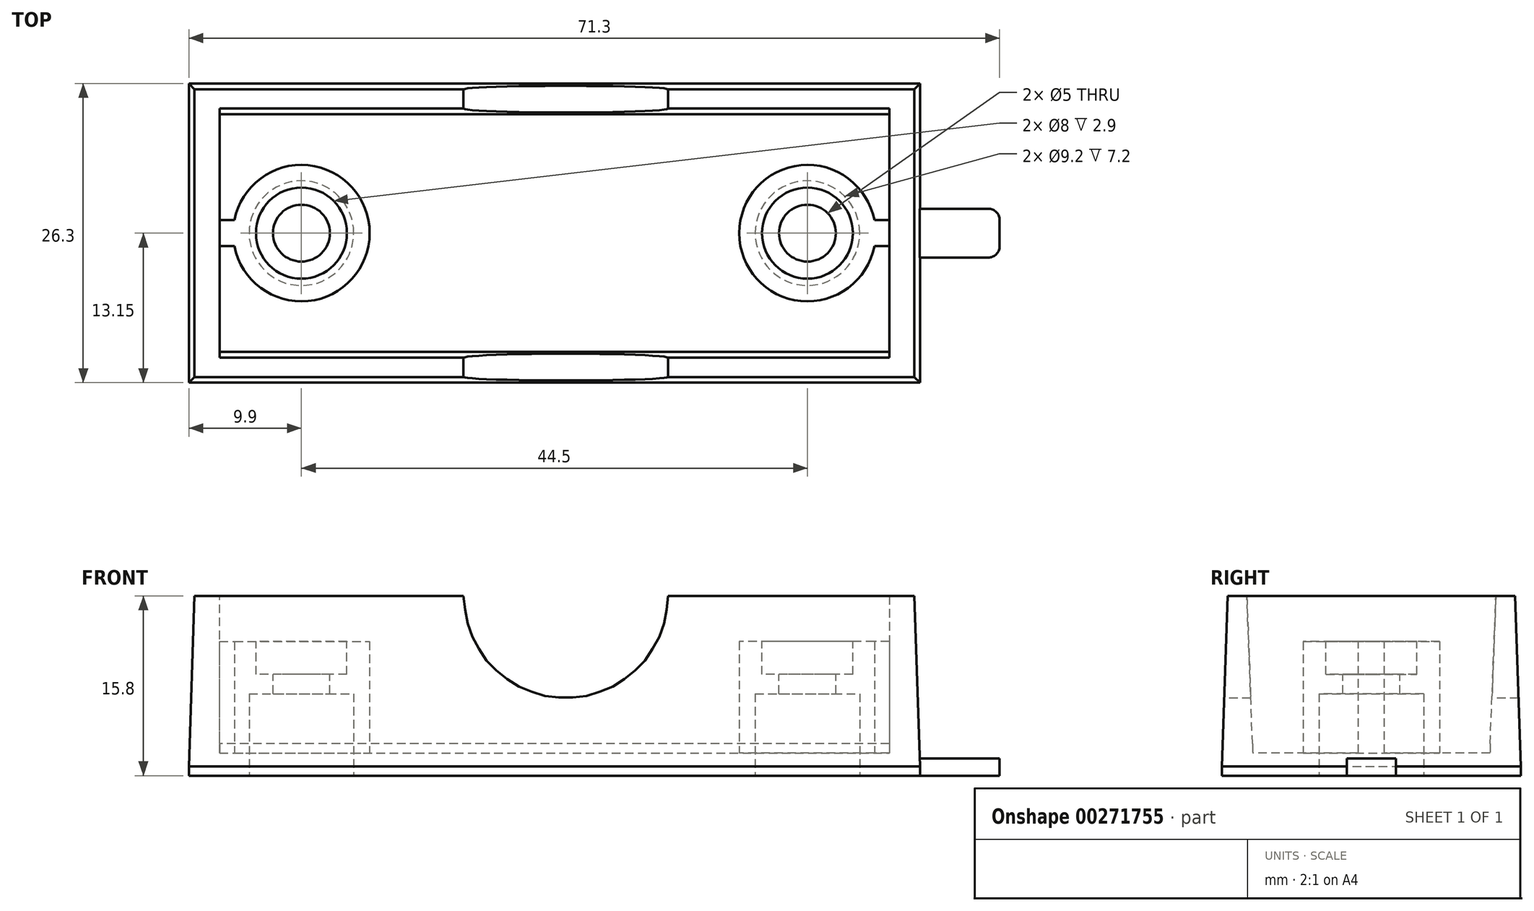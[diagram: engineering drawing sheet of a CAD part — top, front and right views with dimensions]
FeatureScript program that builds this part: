
annotation { "Feature Type Name" : "Feature", "Feature Type Description" : "" }
export const myFeature = defineFeature(function(context is Context, id is Id, definition is map)
    precondition{}
    {
        {
            var Q0;
            Q0=qCreatedBy(makeId("Top.planeOp"),FACE);
            var sketch = newSketch(context, id + "F0", { "sketchPlane" : qUnion([Q0])});
            skLineSegment(sketch, "E0.bottom", {"start": v(-32.15, 13.15) * mm, "end": v(32.15, 13.15) * mm});
            skLineSegment(sketch, "E0.top", {"start": v(-32.15, -13.15) * mm, "end": v(32.15, -13.15) * mm});
            skLineSegment(sketch, "E0.left", {"start": v(-32.15, 13.15) * mm, "end": v(-32.15, -13.15) * mm});
            skLineSegment(sketch, "E0.right", {"start": v(32.15, 13.15) * mm, "end": v(32.15, -13.15) * mm});
            skSolve(sketch);
        }
        {
            var Q0;
            Q0 = qSketchRegion(id + "F0", true);
            extrude(context, id + "F1", {"entities" : qUnion([Q0]), "depth" : 2 * mm});
        }
        {
            var Q0;
            Q0=makeQuery(id+"F1.opExtrude","CAP_FACE",FACE,{"disambiguationData":[OSD([sQuery(id+"F0.wireOp",EDGE,"E0.bottom"),sQuery(id+"F0.wireOp",EDGE,"E0.top"),sQuery(id+"F0.wireOp",EDGE,"E0.left"),sQuery(id+"F0.wireOp",EDGE,"E0.right")])],"isStart":false});
            var sketch = newSketch(context, id + "F2", { "sketchPlane" : qUnion([Q0])});
            skLineSegment(sketch, "E1.bottom", {"start": v(-32.15, 13.15) * mm, "end": v(32.15, 13.15) * mm});
            skLineSegment(sketch, "E1.top", {"start": v(-32.15, -13.15) * mm, "end": v(32.15, -13.15) * mm});
            skLineSegment(sketch, "E1.left", {"start": v(-32.15, 13.15) * mm, "end": v(-32.15, -13.15) * mm});
            skLineSegment(sketch, "E1.right", {"start": v(32.15, 13.15) * mm, "end": v(32.15, -13.15) * mm});
            skLineSegment(sketch, "E2.bottom", {"start": v(-29.45, 10.45) * mm, "end": v(29.45, 10.45) * mm});
            skLineSegment(sketch, "E2.top", {"start": v(-29.45, -10.45) * mm, "end": v(29.45, -10.45) * mm});
            skLineSegment(sketch, "E2.left", {"start": v(-29.45, 10.45) * mm, "end": v(-29.45, -10.45) * mm});
            skLineSegment(sketch, "E2.right", {"start": v(29.45, 10.45) * mm, "end": v(29.45, -10.45) * mm});
            skSolve(sketch);
        }
        {
            var Q0;
            Q0 = qSketchRegion(id + "F2", true);
            extrude(context, id + "F3", {"entities" : qUnion([Q0]), "operationType" : NewBodyOperationType.ADD, "depth" : 13.8 * mm});
        }
        {
            var Q0;
            Q0=makeQuery(id+"F3.boolean.opBoolean","MERGE",FACE,{"derivedFrom":[makeQuery(id+"F1.opExtrude","SWEPT_FACE",FACE,{"disambiguationData":[OSD([sQuery(id+"F0.wireOp",EDGE,"E0.top")])]}),makeQuery(id+"F3.opExtrude","SWEPT_FACE",FACE,{"disambiguationData":[OSD([sQuery(id+"F2.wireOp",EDGE,"E1.top")])]})]});
            var sketch = newSketch(context, id + "F4", { "sketchPlane" : qUnion([Q0])});
            skArc(sketch, "E3", {"start": v(10, 15.8) * mm, "mid": v(1, 6.8) * mm, "end": v(-8, 15.8) * mm});
            skLineSegment(sketch, "E4", {"start": v(-8, 15.8) * mm, "end": v(10, 15.8) * mm});
            skSolve(sketch);
        }
        {
            var Q0;
            Q0 = qSketchRegion(id + "F4", true);
            extrude(context, id + "F5", {"entities" : qUnion([Q0]), "operationType" : NewBodyOperationType.REMOVE, "oppositeDirection" : true, "depth" : 26.5 * mm});
        }
        {
            var Q0;
            Q0=makeQuery(id+"F1.opExtrude","CAP_FACE",FACE,{"disambiguationData":[OSD([sQuery(id+"F0.wireOp",EDGE,"E0.bottom"),sQuery(id+"F0.wireOp",EDGE,"E0.top"),sQuery(id+"F0.wireOp",EDGE,"E0.left"),sQuery(id+"F0.wireOp",EDGE,"E0.right")])],"isStart":false});
            var sketch = newSketch(context, id + "F6", { "sketchPlane" : qUnion([Q0])});
            skCircle(sketch, "E5", {"center": v(-22.25, 0) * mm, "radius": 6 * mm});
            skCircle(sketch, "E6", {"center": v(22.25, 0) * mm, "radius": 6 * mm});
            skLineSegment(sketch, "E7.top", {"start": v(-28.14, -1.15) * mm, "end": v(-29.45, -1.15) * mm});
            skLineSegment(sketch, "E7.left", {"start": v(-28.14, 1.15) * mm, "end": v(-28.14, -1.15) * mm});
            skLineSegment(sketch, "E8.bottom", {"start": v(-30.88, 1.15) * mm, "end": v(-28.14, 1.15) * mm});
            skLineSegment(sketch, "E8.top", {"start": v(-30.88, -1.15) * mm, "end": v(-28.14, -1.15) * mm});
            skLineSegment(sketch, "E8.left", {"start": v(-30.88, 1.15) * mm, "end": v(-30.88, -1.15) * mm});
            skLineSegment(sketch, "E9.bottom", {"start": v(29.95, 1.15) * mm, "end": v(28.14, 1.15) * mm});
            skLineSegment(sketch, "E9.top", {"start": v(29.95, -1.15) * mm, "end": v(28.14, -1.15) * mm});
            skLineSegment(sketch, "E9.left", {"start": v(29.95, 1.15) * mm, "end": v(29.95, -1.15) * mm});
            skLineSegment(sketch, "E9.right", {"start": v(28.14, 1.15) * mm, "end": v(28.14, -1.15) * mm});
            skSolve(sketch);
        }
        {
            var Q0;
            Q0 = qSketchRegion(id + "F6", true);
            extrude(context, id + "F7", {"entities" : qUnion([Q0]), "operationType" : NewBodyOperationType.ADD, "depth" : 9.8 * mm});
        }
        {
            var Q0;
            Q0=makeQuery(id+"F7.opExtrude","CAP_FACE",FACE,{"disambiguationData":[OSD([sQuery(id+"F6.wireOp",EDGE,"E5"),sQuery(id+"F6.wireOp",EDGE,"E8.bottom"),sQuery(id+"F6.wireOp",EDGE,"E8.top"),sQuery(id+"F6.wireOp",EDGE,"E8.left")])],"isStart":false});
            var sketch = newSketch(context, id + "F8", { "sketchPlane" : qUnion([Q0])});
            skCircle(sketch, "E10", {"center": v(-22.25, 0) * mm, "radius": 4 * mm});
            skSolve(sketch);
        }
        {
            var Q0;
            Q0 = qSketchRegion(id + "F8", true);
            extrude(context, id + "F9", {"entities" : qUnion([Q0]), "operationType" : NewBodyOperationType.REMOVE, "oppositeDirection" : true, "depth" : 2.9 * mm});
        }
        {
            var Q0;
            Q0=makeQuery(id+"F7.opExtrude","CAP_FACE",FACE,{"disambiguationData":[OSD([sQuery(id+"F6.wireOp",EDGE,"E6"),sQuery(id+"F6.wireOp",EDGE,"E9.bottom"),sQuery(id+"F6.wireOp",EDGE,"E9.top"),sQuery(id+"F6.wireOp",EDGE,"E9.left")])],"isStart":false});
            var sketch = newSketch(context, id + "F10", { "sketchPlane" : qUnion([Q0])});
            skCircle(sketch, "E11", {"center": v(22.25, 0) * mm, "radius": 4 * mm});
            skSolve(sketch);
        }
        {
            var Q0;
            Q0 = qSketchRegion(id + "F10", true);
            extrude(context, id + "F11", {"entities" : qUnion([Q0]), "operationType" : NewBodyOperationType.REMOVE, "oppositeDirection" : true, "depth" : 2.9 * mm});
        }
        {
            var Q0;
            Q0=makeQuery(id+"F9.boolean.opBoolean","COPY",FACE,{"derivedFrom":makeQuery(id+"F9.opExtrude","CAP_FACE",FACE,{"disambiguationData":[OSD([sQuery(id+"F8.wireOp",EDGE,"E10")])],"isStart":false})});
            var sketch = newSketch(context, id + "F12", { "sketchPlane" : qUnion([Q0])});
            skCircle(sketch, "E12", {"center": v(-22.25, 0) * mm, "radius": 2.5 * mm});
            skSolve(sketch);
        }
        {
            var Q0;
            Q0 = qSketchRegion(id + "F12", true);
            extrude(context, id + "F13", {"entities" : qUnion([Q0]), "operationType" : NewBodyOperationType.REMOVE, "oppositeDirection" : true, "depth" : 9 * mm});
        }
        {
            var Q0;
            Q0=makeQuery(id+"F11.boolean.opBoolean","COPY",FACE,{"derivedFrom":makeQuery(id+"F11.opExtrude","CAP_FACE",FACE,{"disambiguationData":[OSD([sQuery(id+"F10.wireOp",EDGE,"E11")])],"isStart":false})});
            var sketch = newSketch(context, id + "F14", { "sketchPlane" : qUnion([Q0])});
            skCircle(sketch, "E13", {"center": v(22.25, 0) * mm, "radius": 2.5 * mm});
            skSolve(sketch);
        }
        {
            var Q0;
            Q0 = qSketchRegion(id + "F14", true);
            extrude(context, id + "F15", {"entities" : qUnion([Q0]), "operationType" : NewBodyOperationType.REMOVE, "oppositeDirection" : true, "depth" : 9 * mm});
        }
        {
            var Q0;
            Q0=makeQuery(id+"F1.opExtrude","CAP_FACE",FACE,{"disambiguationData":[OSD([sQuery(id+"F0.wireOp",EDGE,"E0.bottom"),sQuery(id+"F0.wireOp",EDGE,"E0.top"),sQuery(id+"F0.wireOp",EDGE,"E0.left"),sQuery(id+"F0.wireOp",EDGE,"E0.right")])],"isStart":true});
            var sketch = newSketch(context, id + "F16", { "sketchPlane" : qUnion([Q0])});
            skCircle(sketch, "E14", {"center": v(-22.25, 0) * mm, "radius": 4.6 * mm});
            skCircle(sketch, "E15", {"center": v(22.25, 0) * mm, "radius": 4.6 * mm});
            skSolve(sketch);
        }
        {
            var Q0;
            Q0 = qSketchRegion(id + "F16", true);
            extrude(context, id + "F17", {"entities" : qUnion([Q0]), "operationType" : NewBodyOperationType.REMOVE, "oppositeDirection" : true, "depth" : 7.2 * mm});
        }
        {
            var Q0;
            {var subQ0=sQuery(id+"F2.wireOp",EDGE,"E1.bottom");Q0=makeQuery(id+"F5.boolean.opBoolean","SPLIT",EDGE,{"disambiguationData":[TD([makeQuery(id+"F1.opExtrude","SWEPT_FACE",FACE,{"disambiguationData":[OSD([sQuery(id+"F0.wireOp",EDGE,"E0.left")])]})])],"derivedFrom":makeQuery(id+"F3.opExtrude","CAP_EDGE",EDGE,{"disambiguationData":[OSD([subQ0])],"isStart":false})});}
            var Q1;
            {var subQ0=sQuery(id+"F2.wireOp",EDGE,"E1.top");Q1=makeQuery(id+"F5.boolean.opBoolean","SPLIT",EDGE,{"disambiguationData":[TD([makeQuery(id+"F1.opExtrude","SWEPT_FACE",FACE,{"disambiguationData":[OSD([sQuery(id+"F0.wireOp",EDGE,"E0.left")])]})])],"derivedFrom":makeQuery(id+"F3.opExtrude","CAP_EDGE",EDGE,{"disambiguationData":[OSD([subQ0])],"isStart":false})});}
            var Q2;
            Q2=makeQuery(id+"F3.opExtrude","CAP_EDGE",EDGE,{"disambiguationData":[OSD([sQuery(id+"F2.wireOp",EDGE,"E1.right")])],"isStart":false});
            var Q3;
            Q3=makeQuery(id+"F3.opExtrude","CAP_EDGE",EDGE,{"disambiguationData":[OSD([sQuery(id+"F2.wireOp",EDGE,"E1.left")])],"isStart":false});
            chamfer(context, id + "F18", {"entities" : qUnion([Q0, Q1, Q2, Q3]), "chamferType" : ChamferType.TWO_OFFSETS, "width1" : 15 * mm, "oppositeDirection" : false, "width2" : .5 * mm, "tangentPropagation" : true});
        }
        {
            var Q0;
            {var subQ0=sQuery(id+"F2.wireOp",EDGE,"E2.right");var subQ1=sQuery(id+"F2.wireOp",EDGE,"E2.top");Q0=makeQuery(id+"F5.boolean.opBoolean","SPLIT",EDGE,{"disambiguationData":[TD([makeQuery(id+"F3.opExtrude","SWEPT_FACE",FACE,{"disambiguationData":[OSD([subQ0])]})])],"derivedFrom":makeQuery(id+"F3.opExtrude","CAP_EDGE",EDGE,{"disambiguationData":[OSD([subQ1])],"isStart":false})});}
            var Q1;
            {var subQ0=sQuery(id+"F2.wireOp",EDGE,"E2.right");var subQ1=sQuery(id+"F2.wireOp",EDGE,"E2.bottom");Q1=makeQuery(id+"F5.boolean.opBoolean","SPLIT",EDGE,{"disambiguationData":[TD([makeQuery(id+"F3.opExtrude","SWEPT_FACE",FACE,{"disambiguationData":[OSD([subQ0])]})])],"derivedFrom":makeQuery(id+"F3.opExtrude","CAP_EDGE",EDGE,{"disambiguationData":[OSD([subQ1])],"isStart":false})});}
            chamfer(context, id + "F19", {"entities" : qUnion([Q0, Q1]), "chamferType" : ChamferType.TWO_OFFSETS, "width1" : 13 * mm, "oppositeDirection" : false, "width2" : .5 * mm, "tangentPropagation" : true});
        }
        {
            var Q0;
            Q0=qCreatedBy(makeId("Top.planeOp"),FACE);
            var sketch = newSketch(context, id + "F20", { "sketchPlane" : qUnion([Q0])});
            skLineSegment(sketch, "E16.bottom", {"start": v(39.15, 2.15) * mm, "end": v(31, 2.15) * mm});
            skLineSegment(sketch, "E16.top", {"start": v(39.15, -2.15) * mm, "end": v(31, -2.15) * mm});
            skLineSegment(sketch, "E16.left", {"start": v(39.15, 2.15) * mm, "end": v(39.15, -2.15) * mm});
            skLineSegment(sketch, "E16.right", {"start": v(31, 2.15) * mm, "end": v(31, -2.15) * mm});
            skSolve(sketch);
        }
        {
            var Q0;
            Q0 = qSketchRegion(id + "F20", true);
            extrude(context, id + "F21", {"entities" : qUnion([Q0]), "operationType" : NewBodyOperationType.ADD, "depth" : 1.5 * mm});
        }
        {
            var Q0;
            Q0=makeQuery(id+"F21.opExtrude","SWEPT_EDGE",EDGE,{"disambiguationData":[OSD([sQuery(id+"F20.wireOp",EDGE,"E16.bottom"),sQuery(id+"F20.wireOp",EDGE,"E16.left")])]});
            var Q1;
            Q1=makeQuery(id+"F21.opExtrude","SWEPT_EDGE",EDGE,{"disambiguationData":[OSD([sQuery(id+"F20.wireOp",EDGE,"E16.top"),sQuery(id+"F20.wireOp",EDGE,"E16.left")])]});
            fillet(context, id + "F22", {"entities" : qUnion([Q0, Q1]), "radius" : 1 * mm, "tangentPropagation" : true, "allowEdgeOverflow" : false});
        }
    });
